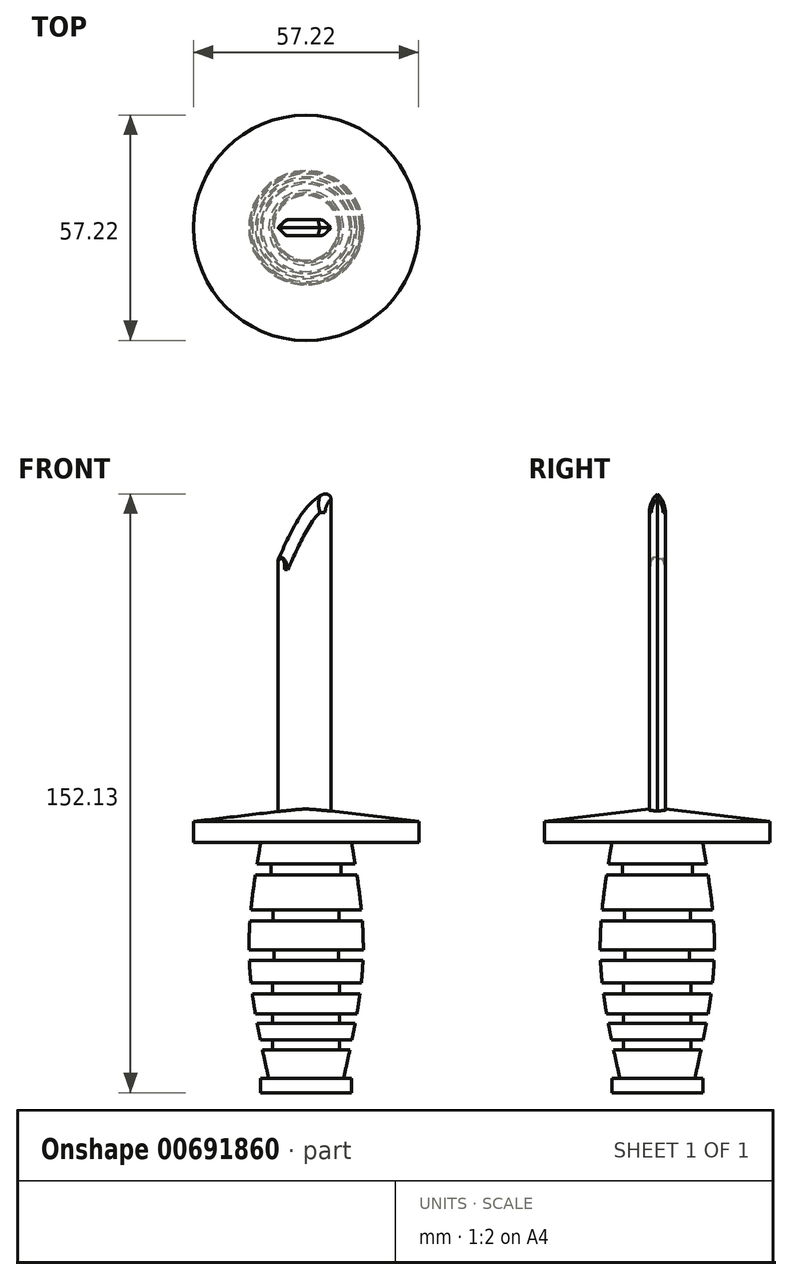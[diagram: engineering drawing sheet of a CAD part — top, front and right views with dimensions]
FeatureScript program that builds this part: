
annotation { "Feature Type Name" : "Feature", "Feature Type Description" : "" }
export const myFeature = defineFeature(function(context is Context, id is Id, definition is map)
    precondition{}
    {
        {
            var Q0;
            Q0=qCreatedBy(makeId("Front.planeOp"),FACE);
            var sketch = newSketch(context, id + "F0", { "sketchPlane" : qUnion([Q0])});
            skLineSegment(sketch, "E0", {"start": v(0, 76.61) * mm, "end": v(0, -78.53) * mm, "construction": true});
            skLineSegment(sketch, "E1.bottom", {"start": v(0, 4.45) * mm, "end": v(19, 4.45) * mm});
            skLineSegment(sketch, "E1.top", {"start": v(0, 0) * mm, "end": v(19, 0) * mm});
            skLineSegment(sketch, "E1.left", {"start": v(0, 4.45) * mm, "end": v(0, 0) * mm});
            skLineSegment(sketch, "E1.right", {"start": v(19, 4.45) * mm, "end": v(19, 0) * mm});
            skPoint(sketch, "E2.2.internal.snap0", {"position": v(9.5, 0) * mm});
            skFitSpline(sketch, "E2", {"points": [v(11.53, 0) * mm, v(14.5, -28.68) * mm, v(9.5, -59.99) * mm], "startDerivative": vector(9.92, -58.16) * mm, "endDerivative": vector(-13.8, -61.78) * mm});
            skLineSegment(sketch, "E3.bottom", {"start": v(11.53, -59.99) * mm, "end": v(0, -59.99) * mm});
            skLineSegment(sketch, "E3.top", {"start": v(11.53, -63.56) * mm, "end": v(0, -63.56) * mm});
            skLineSegment(sketch, "E3.left", {"start": v(11.53, -59.99) * mm, "end": v(11.53, -63.56) * mm});
            skLineSegment(sketch, "E3.right", {"start": v(0, -59.99) * mm, "end": v(0, -63.56) * mm});
            skLineSegment(sketch, "E4", {"start": v(0, -59.99) * mm, "end": v(0, 0) * mm});
            skLineSegment(sketch, "E5", {"start": v(0, -9.82) * mm, "end": v(0, -35.83) * mm});
            skSolve(sketch);
        }
        {
            var Q0;
            Q0 = qSketchRegion(id + "F0", true);
            var Q1;
            Q1=sQuery(id+"F0.wireOp",EDGE,"E5");
            revolve(context, id + "F1", {"entities" : qUnion([Q0]), "axis" : qUnion([Q1]), "revolveType" : RevolveType.FULL});
        }
        {
            var Q0;
            Q0=qCreatedBy(makeId("Front.planeOp"),FACE);
            var sketch = newSketch(context, id + "F2", { "sketchPlane" : qUnion([Q0])});
            skLineSegment(sketch, "E6.bottom", {"start": v(15.86, -5.5) * mm, "end": v(8.9, -5.5) * mm});
            skLineSegment(sketch, "E6.top", {"start": v(15.86, -8.28) * mm, "end": v(8.9, -8.28) * mm});
            skLineSegment(sketch, "E6.left", {"start": v(15.86, -5.5) * mm, "end": v(15.86, -8.28) * mm});
            skLineSegment(sketch, "E6.right", {"start": v(8.9, -5.5) * mm, "end": v(8.9, -8.28) * mm});
            skLineSegment(sketch, "E7.bottom", {"start": v(15.86, -17.17) * mm, "end": v(8.37, -17.17) * mm});
            skLineSegment(sketch, "E7.top", {"start": v(15.86, -19.96) * mm, "end": v(8.37, -19.96) * mm});
            skLineSegment(sketch, "E7.left", {"start": v(15.86, -17.17) * mm, "end": v(15.86, -19.96) * mm});
            skLineSegment(sketch, "E7.right", {"start": v(8.37, -17.17) * mm, "end": v(8.37, -19.96) * mm});
            skLineSegment(sketch, "E8.bottom", {"start": v(15.86, -27.28) * mm, "end": v(8.2, -27.28) * mm});
            skLineSegment(sketch, "E8.top", {"start": v(15.86, -29.9) * mm, "end": v(8.2, -29.9) * mm});
            skLineSegment(sketch, "E8.left", {"start": v(15.86, -27.28) * mm, "end": v(15.86, -29.9) * mm});
            skLineSegment(sketch, "E8.right", {"start": v(8.2, -27.28) * mm, "end": v(8.2, -29.9) * mm});
            skLineSegment(sketch, "E9.bottom", {"start": v(15.86, -35.65) * mm, "end": v(8.54, -35.65) * mm});
            skLineSegment(sketch, "E9.top", {"start": v(15.86, -38.44) * mm, "end": v(8.54, -38.44) * mm});
            skLineSegment(sketch, "E9.left", {"start": v(15.86, -35.65) * mm, "end": v(15.86, -38.44) * mm});
            skLineSegment(sketch, "E9.right", {"start": v(8.54, -35.65) * mm, "end": v(8.54, -38.44) * mm});
            skLineSegment(sketch, "E10.bottom", {"start": v(15.86, -43.5) * mm, "end": v(8.54, -43.5) * mm});
            skLineSegment(sketch, "E10.top", {"start": v(15.86, -45.93) * mm, "end": v(8.54, -45.93) * mm});
            skLineSegment(sketch, "E10.left", {"start": v(15.86, -43.5) * mm, "end": v(15.86, -45.93) * mm});
            skLineSegment(sketch, "E10.right", {"start": v(8.54, -43.5) * mm, "end": v(8.54, -45.93) * mm});
            skLineSegment(sketch, "E11.bottom", {"start": v(15.86, -50.12) * mm, "end": v(8.54, -50.12) * mm});
            skLineSegment(sketch, "E11.top", {"start": v(15.86, -52.73) * mm, "end": v(8.54, -52.73) * mm});
            skLineSegment(sketch, "E11.left", {"start": v(15.86, -50.12) * mm, "end": v(15.86, -52.73) * mm});
            skLineSegment(sketch, "E11.right", {"start": v(8.54, -50.12) * mm, "end": v(8.54, -52.73) * mm});
            skSolve(sketch);
        }
        {
            var Q0;
            Q0 = qSketchRegion(id + "F2", true);
            var Q1;
            Q1=sQuery(id+"F0.wireOp",EDGE,"E0");
            revolve(context, id + "F3", {"operationType" : NewBodyOperationType.REMOVE, "entities" : qUnion([Q0]), "axis" : qUnion([Q1]), "revolveType" : RevolveType.FULL, "oppositeDirection" : true});
        }
        {
            var Q0;
            Q0=qCreatedBy(makeId("Front.planeOp"),FACE);
            var sketch = newSketch(context, id + "F4", { "sketchPlane" : qUnion([Q0])});
            skLineSegment(sketch, "E12", {"start": v(-7.15, 2) * mm, "end": v(-7.15, 72.78) * mm});
            skLineSegment(sketch, "E13", {"start": v(-7.15, 2) * mm, "end": v(6.32, 2) * mm});
            skLineSegment(sketch, "E14", {"start": v(6.32, 2) * mm, "end": v(6.32, 90.22) * mm});
            skFitSpline(sketch, "E15", {"points": [v(-7.15, 72.78) * mm, v(0, 85.53) * mm, v(6.32, 90.22) * mm], "startDerivative": vector(11.66, 25.3) * mm, "endDerivative": vector(15.48, 8.75) * mm});
            skSolve(sketch);
        }
        {
            var Q0;
            Q0 = qSketchRegion(id + "F4", true);
            extrude(context, id + "F5", {"entities" : qUnion([Q0]), "operationType" : NewBodyOperationType.ADD, "endBound" : BoundingType.SYMMETRIC, "depth" : 4.06 * mm, "offsetDistance" : 25.4 * mm});
        }
        {
            var Q0;
            Q0=makeQuery(id+"F5.opExtrude","CAP_EDGE",EDGE,{"disambiguationData":[OSD([sQuery(id+"F4.wireOp",EDGE,"E12")])],"isStart":false});
            var Q1;
            Q1=makeQuery(id+"F5.opExtrude","CAP_EDGE",EDGE,{"disambiguationData":[OSD([sQuery(id+"F4.wireOp",EDGE,"E12")])],"isStart":true});
            var Q2;
            Q2=makeQuery(id+"F5.opExtrude","CAP_EDGE",EDGE,{"disambiguationData":[OSD([sQuery(id+"F4.wireOp",EDGE,"E14")])],"isStart":true});
            var Q3;
            Q3=makeQuery(id+"F5.opExtrude","CAP_EDGE",EDGE,{"disambiguationData":[OSD([sQuery(id+"F4.wireOp",EDGE,"E14")])],"isStart":false});
            chamfer(context, id + "F6", {"entities" : qUnion([Q0, Q1, Q2, Q3]), "width" : 2.03 * mm, "tangentPropagation" : true});
        }
        {
            var Q0;
            Q0=makeQuery(id+"F5.opExtrude","CAP_EDGE",EDGE,{"disambiguationData":[OSD([sQuery(id+"F4.wireOp",EDGE,"E15")])],"isStart":false});
            var Q1;
            Q1=makeQuery(id+"F5.opExtrude","CAP_EDGE",EDGE,{"disambiguationData":[OSD([sQuery(id+"F4.wireOp",EDGE,"E15")])],"isStart":true});
            fillet(context, id + "F7", {"entities" : qUnion([Q0, Q1]), "radius" : 3.68 * mm, "tangentPropagation" : true, "allowEdgeOverflow" : false});
        }
        {
            var Q0;
            {var subQ0=sQuery(id+"F4.wireOp",EDGE,"E12");Q0=makeQuery(id+"F7.opFillet","BLEND_EDGE",EDGE,{"blendedFrom":[makeQuery(id+"F5.opExtrude","CAP_EDGE",EDGE,{"disambiguationData":[OSD([sQuery(id+"F4.wireOp",EDGE,"E15")])],"isStart":false}),makeQuery(id+"F6.opChamfer","BLEND_FACE",FACE,{"disambiguationData":[OSD([subQ0]),TDD([makeQuery(id+"F5.opExtrude","CAP_EDGE",EDGE,{"disambiguationData":[OSD([subQ0])],"isStart":false})])]})],"blendedInto":[makeQuery(id+"F6.opChamfer","BLEND_FACE",FACE,{"disambiguationData":[OSD([subQ0]),TDD([makeQuery(id+"F5.opExtrude","CAP_EDGE",EDGE,{"disambiguationData":[OSD([subQ0])],"isStart":false})])]})]});}
            var Q1;
            {var subQ0=sQuery(id+"F4.wireOp",EDGE,"E12");Q1=makeQuery(id+"F7.opFillet","BLEND_EDGE",EDGE,{"blendedFrom":[makeQuery(id+"F5.opExtrude","CAP_EDGE",EDGE,{"disambiguationData":[OSD([sQuery(id+"F4.wireOp",EDGE,"E15")])],"isStart":true}),makeQuery(id+"F6.opChamfer","BLEND_FACE",FACE,{"disambiguationData":[OSD([subQ0]),TDD([makeQuery(id+"F5.opExtrude","CAP_EDGE",EDGE,{"disambiguationData":[OSD([subQ0])],"isStart":true})])]})],"blendedInto":[makeQuery(id+"F6.opChamfer","BLEND_FACE",FACE,{"disambiguationData":[OSD([subQ0]),TDD([makeQuery(id+"F5.opExtrude","CAP_EDGE",EDGE,{"disambiguationData":[OSD([subQ0])],"isStart":true})])]})]});}
            fillet(context, id + "F8", {"entities" : qUnion([Q0, Q1]), "radius" : 1.07 * mm, "tangentPropagation" : true, "allowEdgeOverflow" : false});
        }
        {
            var Q0;
            {var subQ0=sQuery(id+"F4.wireOp",EDGE,"E14");Q0=makeQuery(id+"F7.opFillet","BLEND_EDGE",EDGE,{"blendedFrom":[makeQuery(id+"F5.opExtrude","CAP_EDGE",EDGE,{"disambiguationData":[OSD([sQuery(id+"F4.wireOp",EDGE,"E15")])],"isStart":false}),makeQuery(id+"F6.opChamfer","BLEND_FACE",FACE,{"disambiguationData":[OSD([subQ0]),TDD([makeQuery(id+"F5.opExtrude","CAP_EDGE",EDGE,{"disambiguationData":[OSD([subQ0])],"isStart":false})])]})],"blendedInto":[makeQuery(id+"F6.opChamfer","BLEND_FACE",FACE,{"disambiguationData":[OSD([subQ0]),TDD([makeQuery(id+"F5.opExtrude","CAP_EDGE",EDGE,{"disambiguationData":[OSD([subQ0])],"isStart":false})])]})]});}
            var Q1;
            {var subQ0=sQuery(id+"F4.wireOp",EDGE,"E14");Q1=makeQuery(id+"F7.opFillet","BLEND_EDGE",EDGE,{"blendedFrom":[makeQuery(id+"F5.opExtrude","CAP_EDGE",EDGE,{"disambiguationData":[OSD([sQuery(id+"F4.wireOp",EDGE,"E15")])],"isStart":true}),makeQuery(id+"F6.opChamfer","BLEND_FACE",FACE,{"disambiguationData":[OSD([subQ0]),TDD([makeQuery(id+"F5.opExtrude","CAP_EDGE",EDGE,{"disambiguationData":[OSD([subQ0])],"isStart":true})])]})],"blendedInto":[makeQuery(id+"F6.opChamfer","BLEND_FACE",FACE,{"disambiguationData":[OSD([subQ0]),TDD([makeQuery(id+"F5.opExtrude","CAP_EDGE",EDGE,{"disambiguationData":[OSD([subQ0])],"isStart":true})])]})]});}
            fillet(context, id + "F9", {"entities" : qUnion([Q0, Q1]), "radius" : 1.88 * mm, "tangentPropagation" : true, "allowEdgeOverflow" : false});
        }
        {
            var Q0;
            Q0=qCreatedBy(makeId("Front.planeOp"),FACE);
            var sketch = newSketch(context, id + "F10", { "sketchPlane" : qUnion([Q0])});
            skLineSegment(sketch, "E16", {"start": v(0, 91.45) * mm, "end": v(0, -74) * mm, "construction": true});
            skLineSegment(sketch, "E17", {"start": v(0, 8.72) * mm, "end": v(-28.61, 5.34) * mm});
            skLineSegment(sketch, "E18", {"start": v(-28.61, 5.34) * mm, "end": v(-28.61, 0) * mm});
            skLineSegment(sketch, "E19", {"start": v(-28.61, 0) * mm, "end": v(0, 0) * mm});
            skLineSegment(sketch, "E20", {"start": v(0, 0) * mm, "end": v(0, 8.72) * mm});
            skSolve(sketch);
        }
        {
            var Q0;
            Q0 = qSketchRegion(id + "F10", true);
            var Q1;
            Q1=sQuery(id+"F10.wireOp",EDGE,"E20");
            revolve(context, id + "F11", {"operationType" : NewBodyOperationType.ADD, "entities" : qUnion([Q0]), "axis" : qUnion([Q1]), "revolveType" : RevolveType.FULL});
        }
    });
